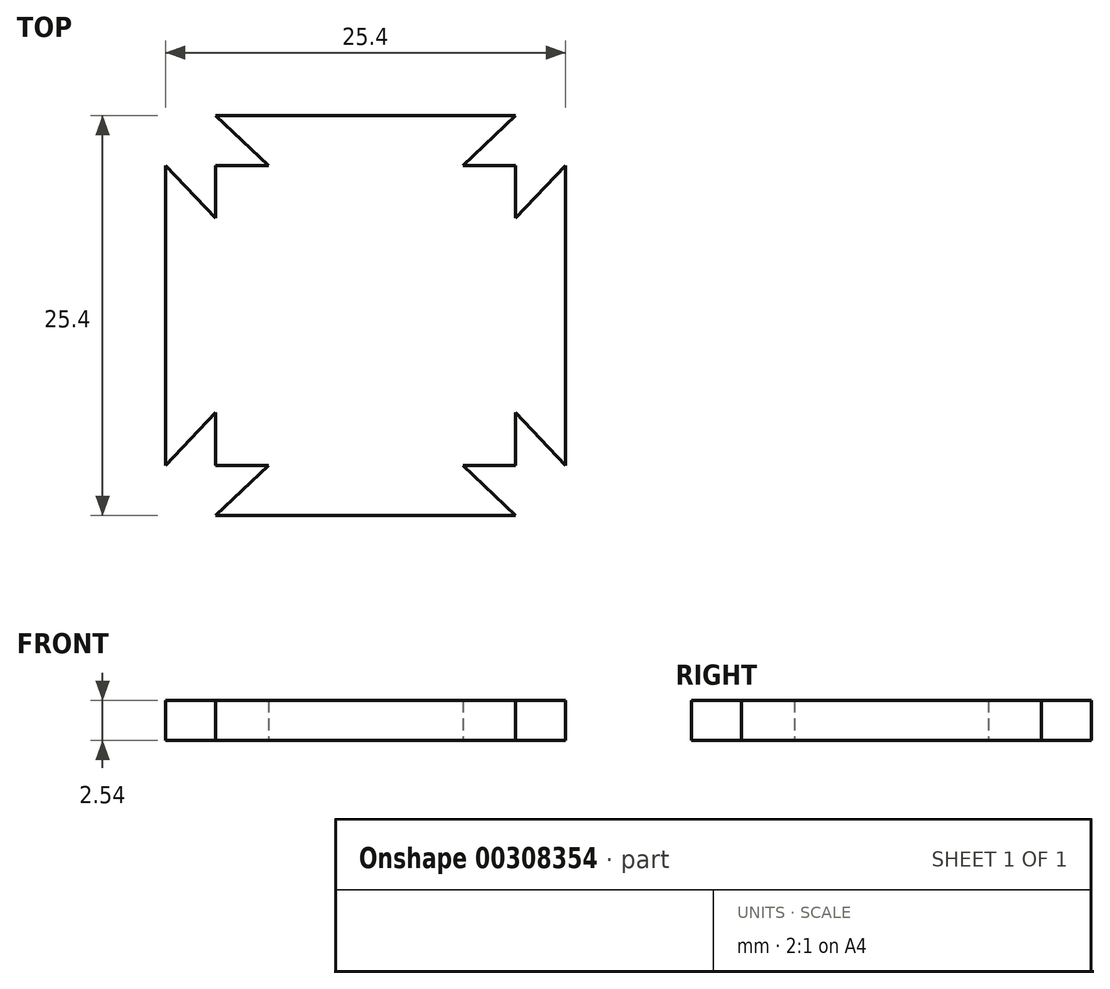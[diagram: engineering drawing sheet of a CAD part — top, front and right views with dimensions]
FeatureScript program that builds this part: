
annotation { "Feature Type Name" : "Feature", "Feature Type Description" : "" }
export const myFeature = defineFeature(function(context is Context, id is Id, definition is map)
    precondition{}
    {
        {
            var Q0;
            Q0=qCreatedBy(makeId("Top.planeOp"),FACE);
            var sketch = newSketch(context, id + "F0", { "sketchPlane" : qUnion([Q0])});
            skLineSegment(sketch, "E0.bottom", {"start": v(-35.57, 17.8) * mm, "end": v(-16.52, 17.8) * mm});
            skLineSegment(sketch, "E0.top", {"start": v(-35.57, -1.25) * mm, "end": v(-16.52, -1.25) * mm});
            skLineSegment(sketch, "E0.left", {"start": v(-35.57, 17.8) * mm, "end": v(-35.57, -1.25) * mm});
            skLineSegment(sketch, "E0.right", {"start": v(-16.52, 17.8) * mm, "end": v(-16.52, -1.25) * mm});
            skLineSegment(sketch, "E1", {"start": v(-13.35, 17.8) * mm, "end": v(-13.35, -1.25) * mm});
            skLineSegment(sketch, "E2", {"start": v(-35.57, -4.43) * mm, "end": v(-16.52, -4.43) * mm});
            skLineSegment(sketch, "E3", {"start": v(-38.75, -1.25) * mm, "end": v(-38.75, 17.8) * mm});
            skPoint(sketch, "E3.endSnap0", {"position": v(-26.05, 17.8) * mm});
            skLineSegment(sketch, "E4", {"start": v(-35.57, 20.97) * mm, "end": v(-16.52, 20.97) * mm});
            skLineSegment(sketch, "E5", {"start": v(-35.57, 17.8) * mm, "end": v(-32.22, 17.8) * mm});
            skLineSegment(sketch, "E6", {"start": v(-16.52, 17.8) * mm, "end": v(-19.88, 17.8) * mm});
            skLineSegment(sketch, "E7", {"start": v(-16.52, 17.8) * mm, "end": v(-16.52, 14.44) * mm});
            skLineSegment(sketch, "E8", {"start": v(-16.52, -1.25) * mm, "end": v(-16.52, 2.1) * mm});
            skLineSegment(sketch, "E9", {"start": v(-16.52, -1.25) * mm, "end": v(-19.88, -1.25) * mm});
            skLineSegment(sketch, "E10", {"start": v(-35.57, -1.25) * mm, "end": v(-32.22, -1.25) * mm});
            skLineSegment(sketch, "E11", {"start": v(-35.57, 17.8) * mm, "end": v(-35.57, 14.44) * mm});
            skLineSegment(sketch, "E12", {"start": v(-35.57, 14.44) * mm, "end": v(-38.75, 17.8) * mm});
            skLineSegment(sketch, "E13", {"start": v(-35.57, -1.25) * mm, "end": v(-35.57, 2.1) * mm});
            skLineSegment(sketch, "E14", {"start": v(-35.57, 2.1) * mm, "end": v(-38.75, -1.25) * mm});
            skLineSegment(sketch, "E15", {"start": v(-32.22, -1.25) * mm, "end": v(-35.57, -4.43) * mm});
            skLineSegment(sketch, "E16", {"start": v(-19.88, -1.25) * mm, "end": v(-16.52, -4.43) * mm});
            skLineSegment(sketch, "E17", {"start": v(-16.52, 2.1) * mm, "end": v(-13.35, -1.25) * mm});
            skLineSegment(sketch, "E18", {"start": v(-16.52, 14.44) * mm, "end": v(-13.35, 17.8) * mm});
            skLineSegment(sketch, "E19", {"start": v(-19.88, 17.8) * mm, "end": v(-16.52, 20.97) * mm});
            skLineSegment(sketch, "E20", {"start": v(-32.22, 17.8) * mm, "end": v(-35.57, 20.97) * mm});
            skSolve(sketch);
        }
        {
            var Q0;
            Q0=qSketchRegion(id+"F0",true);
            extrude(context, id + "F1", {"entities" : qUnion([Q0]), "depth" : 2.54 * mm});
        }
    });
